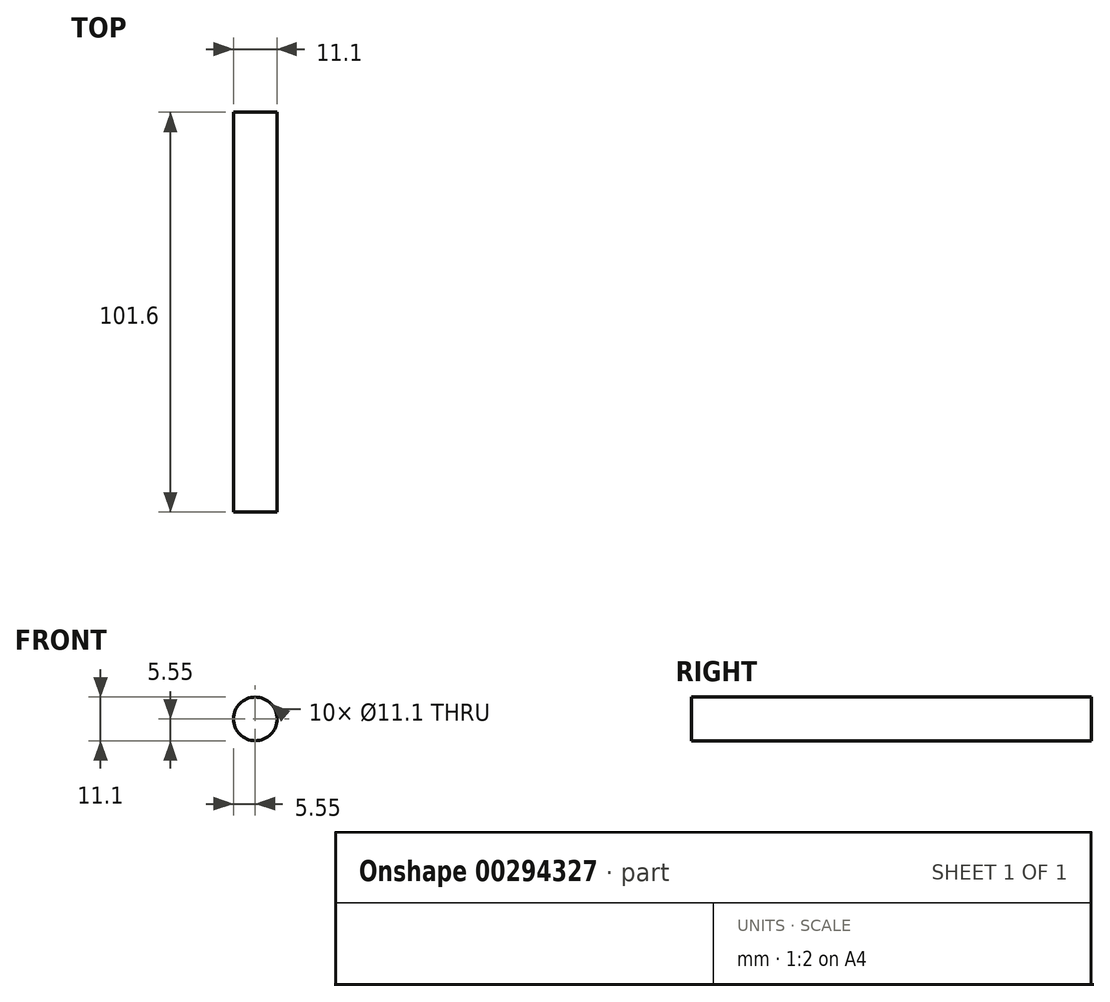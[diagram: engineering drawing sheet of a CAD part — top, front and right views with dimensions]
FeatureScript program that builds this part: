
annotation { "Feature Type Name" : "Feature", "Feature Type Description" : "" }
export const myFeature = defineFeature(function(context is Context, id is Id, definition is map)
    precondition{}
    {
        {
            var Q0;
            Q0=qCreatedBy(makeId("Front.planeOp"),FACE);
            var sketch = newSketch(context, id + "F0", { "sketchPlane" : qUnion([Q0])});
            skCircle(sketch, "E0", {"center": v(0, 0) * mm, "radius": 5.55 * mm});
            skCircle(sketch, "E1", {"center": v(0, 0) * mm, "radius": 4.76 * mm});
            skSolve(sketch);
        }
        {
            var Q0;
            Q0=sQuery(id+"F0.wireOp",EDGE,"E0");
            extrude(context, id + "F1", {"bodyType" : ToolBodyType.SURFACE, "surfaceEntities" : qUnion([Q0]), "oppositeDirection" : true, "depth" : 101.6 * mm});
        }
    });
